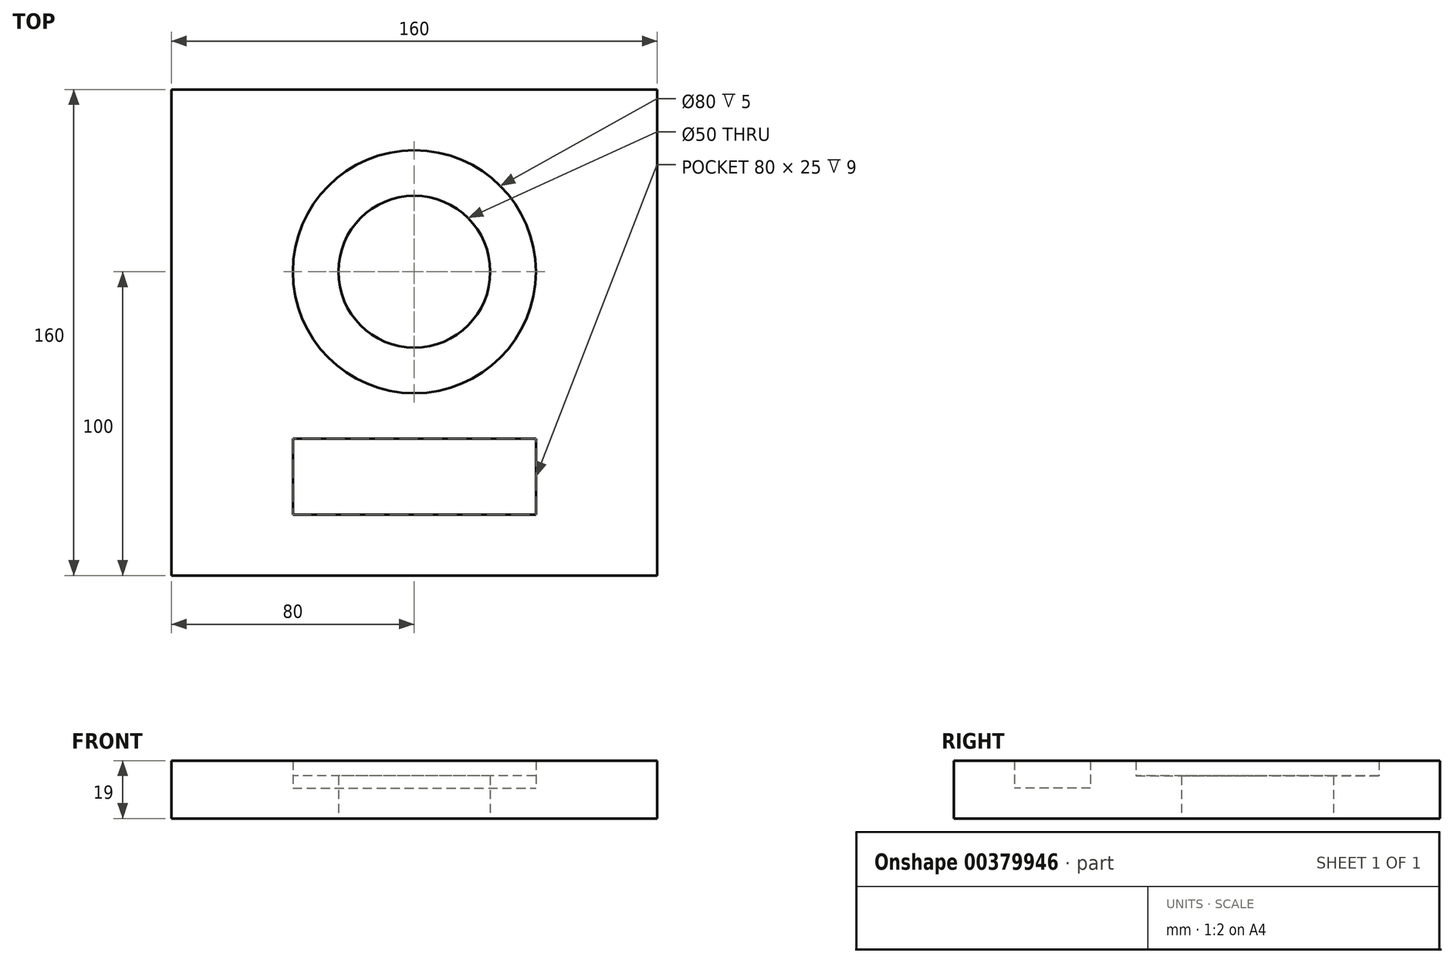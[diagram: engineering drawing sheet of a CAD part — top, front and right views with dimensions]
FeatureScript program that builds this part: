
annotation { "Feature Type Name" : "Feature", "Feature Type Description" : "" }
export const myFeature = defineFeature(function(context is Context, id is Id, definition is map)
    precondition{}
    {
        {
            var Q0;
            Q0=qCreatedBy(makeId("Top.planeOp"),FACE);
            var sketch = newSketch(context, id + "F0", { "sketchPlane" : qUnion([Q0])});
            skLineSegment(sketch, "E0.bottom", {"start": v(0, 0) * mm, "end": v(160, 0) * mm});
            skLineSegment(sketch, "E0.top", {"start": v(0, 160) * mm, "end": v(160, 160) * mm});
            skLineSegment(sketch, "E0.left", {"start": v(0, 0) * mm, "end": v(0, 160) * mm});
            skLineSegment(sketch, "E0.right", {"start": v(160, 0) * mm, "end": v(160, 160) * mm});
            skCircle(sketch, "E1", {"center": v(80, 100) * mm, "radius": 40 * mm});
            skCircle(sketch, "E2.0", {"center": v(80, 100) * mm, "radius": 25 * mm});
            skLineSegment(sketch, "E3.bottom", {"start": v(40, 45) * mm, "end": v(120, 45) * mm});
            skLineSegment(sketch, "E3.top", {"start": v(40, 20) * mm, "end": v(120, 20) * mm});
            skLineSegment(sketch, "E3.left", {"start": v(40, 45) * mm, "end": v(40, 20) * mm});
            skLineSegment(sketch, "E3.right", {"start": v(120, 45) * mm, "end": v(120, 20) * mm});
            skSolve(sketch);
        }
        {
            var Q0;
            Q0 = qSketchRegion(id + "F0", true);
            extrude(context, id + "F1", {"entities" : qUnion([Q0]), "depth" : 19 * mm});
        }
        {
            var Q0;
            Q0=makeQuery(id+"F0.imprint","IMPRINT",FACE,{"disambiguationData":[TD([[makeQuery(id+"F0.imprint","IMPRINT",EDGE,{"derivedFrom":sQuery(id+"F0.wireOp",EDGE,"E1")}),1.0]])]});
            extrude(context, id + "F2", {"entities" : qUnion([Q0]), "operationType" : NewBodyOperationType.ADD, "depth" : 14 * mm});
        }
        {
            var Q0;
            Q0=makeQuery(id+"F0.imprint","IMPRINT",FACE,{"disambiguationData":[TD([[makeQuery(id+"F0.imprint","IMPRINT",EDGE,{"derivedFrom":sQuery(id+"F0.wireOp",EDGE,"E3.bottom")}),-1.0]])]});
            extrude(context, id + "F3", {"entities" : qUnion([Q0]), "operationType" : NewBodyOperationType.ADD, "depth" : 10 * mm});
        }
    });
